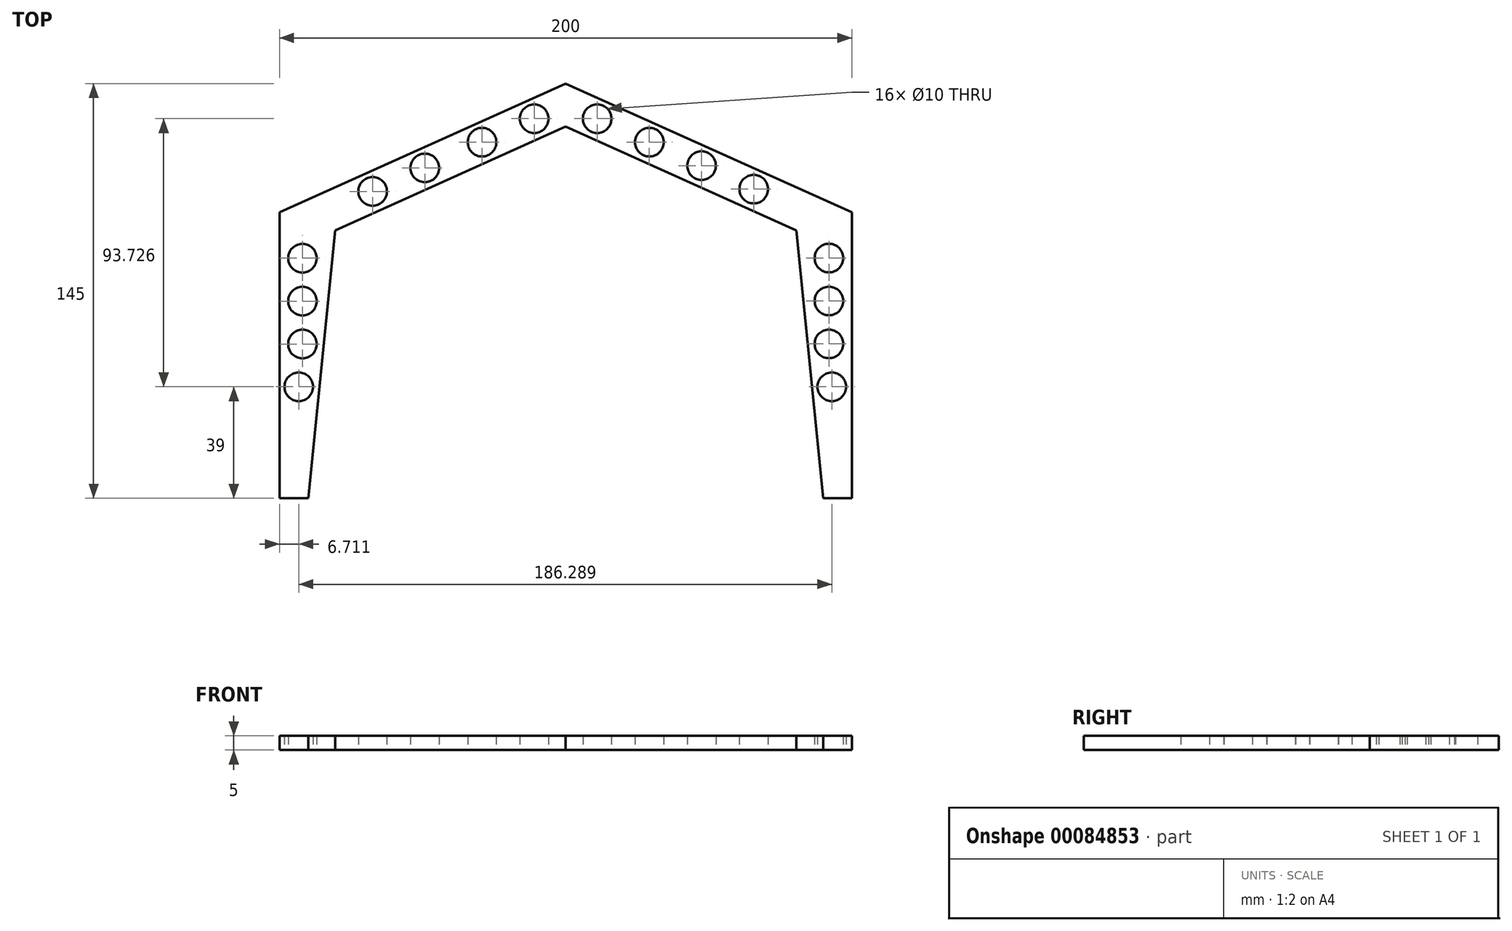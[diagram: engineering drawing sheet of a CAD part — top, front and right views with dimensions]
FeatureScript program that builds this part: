
annotation { "Feature Type Name" : "Feature", "Feature Type Description" : "" }
export const myFeature = defineFeature(function(context is Context, id is Id, definition is map)
    precondition{}
    {
        {
            var Q0;
            Q0=qCreatedBy(makeId("Top.planeOp"),FACE);
            var sketch = newSketch(context, id + "F0", { "sketchPlane" : qUnion([Q0])});
            skLineSegment(sketch, "E0", {"start": v(0, 0) * mm, "end": v(0, 130) * mm});
            skLineSegment(sketch, "E1", {"start": v(0, 130) * mm, "end": v(0, 145) * mm});
            skLineSegment(sketch, "E2", {"start": v(0, 0) * mm, "end": v(100, 0) * mm});
            skLineSegment(sketch, "E3", {"start": v(0, 0) * mm, "end": v(-100, 0) * mm});
            skLineSegment(sketch, "E4", {"start": v(-100, 0) * mm, "end": v(-100, 100) * mm});
            skLineSegment(sketch, "E5", {"start": v(100, 0) * mm, "end": v(100, 100) * mm});
            skLineSegment(sketch, "E6", {"start": v(90, 0) * mm, "end": v(80, 100) * mm});
            skLineSegment(sketch, "E7", {"start": v(100, 100) * mm, "end": v(80, 100) * mm});
            skLineSegment(sketch, "E8", {"start": v(-90, 0) * mm, "end": v(-80, 99.86) * mm});
            skLineSegment(sketch, "E9", {"start": v(-80, 99.86) * mm, "end": v(-100, 100) * mm});
            skLineSegment(sketch, "E10", {"start": v(-100, 100) * mm, "end": v(0, 145) * mm});
            skLineSegment(sketch, "E11", {"start": v(0, 145) * mm, "end": v(100, 100) * mm});
            skLineSegment(sketch, "E12", {"start": v(0, 130) * mm, "end": v(80.63, 93.72) * mm});
            skLineSegment(sketch, "E13", {"start": v(0, 130) * mm, "end": v(-80.62, 93.72) * mm});
            skCircle(sketch, "E14", {"center": v(-92, 83.94) * mm, "radius": 5 * mm});
            skCircle(sketch, "E15", {"center": v(-92, 68.94) * mm, "radius": 5 * mm});
            skCircle(sketch, "E16", {"center": v(-92, 53.94) * mm, "radius": 5 * mm});
            skCircle(sketch, "E17", {"center": v(-93.29, 39) * mm, "radius": 5 * mm});
            skCircle(sketch, "E18", {"center": v(92, 84) * mm, "radius": 5 * mm});
            skCircle(sketch, "E19", {"center": v(92, 69) * mm, "radius": 5 * mm});
            skCircle(sketch, "E20", {"center": v(92, 54) * mm, "radius": 5 * mm});
            skCircle(sketch, "E21", {"center": v(93, 39) * mm, "radius": 5 * mm});
            skCircle(sketch, "E22", {"center": v(-67.48, 107.3) * mm, "radius": 5 * mm});
            skCircle(sketch, "E23", {"center": v(-49.24, 115.52) * mm, "radius": 5 * mm});
            skCircle(sketch, "E24", {"center": v(-29.24, 124.52) * mm, "radius": 5 * mm});
            skCircle(sketch, "E25", {"center": v(-11, 132.73) * mm, "radius": 5 * mm});
            skCircle(sketch, "E26", {"center": v(11, 132.73) * mm, "radius": 5 * mm});
            skCircle(sketch, "E27", {"center": v(29.24, 124.52) * mm, "radius": 5 * mm});
            skCircle(sketch, "E28", {"center": v(47.48, 116.31) * mm, "radius": 5 * mm});
            skCircle(sketch, "E29", {"center": v(65.72, 108.1) * mm, "radius": 5 * mm});
            skSolve(sketch);
        }
        {
            var Q0;
            {var subQ5=sQuery(id+"F0.wireOp",EDGE,"E5");Q0=makeQuery(id+"F0.imprint","IMPRINT",FACE,{"disambiguationData":[TD([[makeQuery(id+"F0.imprint","IMPRINT",EDGE,{"derivedFrom":subQ5}),1.0]])]});}
            var Q1;
            {var subQ3=sQuery(id+"F0.wireOp",EDGE,"E4");Q1=makeQuery(id+"F0.imprint","IMPRINT",FACE,{"disambiguationData":[TD([[makeQuery(id+"F0.imprint","IMPRINT",EDGE,{"derivedFrom":subQ3}),-1.0]])]});}
            var Q2;
            Q2=makeQuery(id+"F0.imprint","IMPRINT",FACE,{"disambiguationData":[TD([[makeQuery(id+"F0.imprint","IMPRINT",EDGE,{"derivedFrom":sQuery(id+"F0.wireOp",EDGE,"E1")}),-1.0]])]});
            var Q3;
            Q3=makeQuery(id+"F0.imprint","IMPRINT",FACE,{"disambiguationData":[TD([[makeQuery(id+"F0.imprint","IMPRINT",EDGE,{"derivedFrom":sQuery(id+"F0.wireOp",EDGE,"E1")}),1.0]])]});
            extrude(context, id + "F1", {"entities" : qUnion([Q0, Q1, Q2, Q3]), "depth" : 5 * mm});
        }
    });
